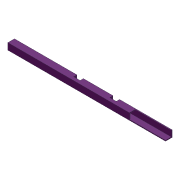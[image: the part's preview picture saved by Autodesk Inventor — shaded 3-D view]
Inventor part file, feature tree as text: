
AUTODESK INVENTOR PART (.ipt)
format: ipt  version: 2012 (Build 160160000, 160)  size: 104,960 bytes
history: native  units: in
note: dims shown in document units (in); Inventor stores cm internally (conversion verified against a paired STEP export)
features: extrude x3, sketch x3, shell x1
ambient origin geometry x8: Origin, YZ Plane, XZ Plane, XY Plane, X Axis, Y Axis, Z Axis, Center Point
bodies: Solid1 (feature_tree)
feature tree (7):
  extrude  "Extrusion1"  Depth=24.0in
  shell  "Shell2"  Thickness=1.0in
  extrude  "Extrusion3"  Depth=0.875in
  extrude  "Extrusion4"  Depth=0.875in TaperAngle=0.0deg
  sketch  "Sketch1"  dims[d0=1.0in d1=24.0in d2=1.0in d3=0.0in]
  sketch  "Sketch3"  dims[d8=0.125in d9=0.875in]
  sketch  "Sketch4"  dims[d10=5.5in d11=0.875in d12=0.0in d13=0.5in d14=1.0in d16=0.875in d17=0.0in d18=4.5in]
